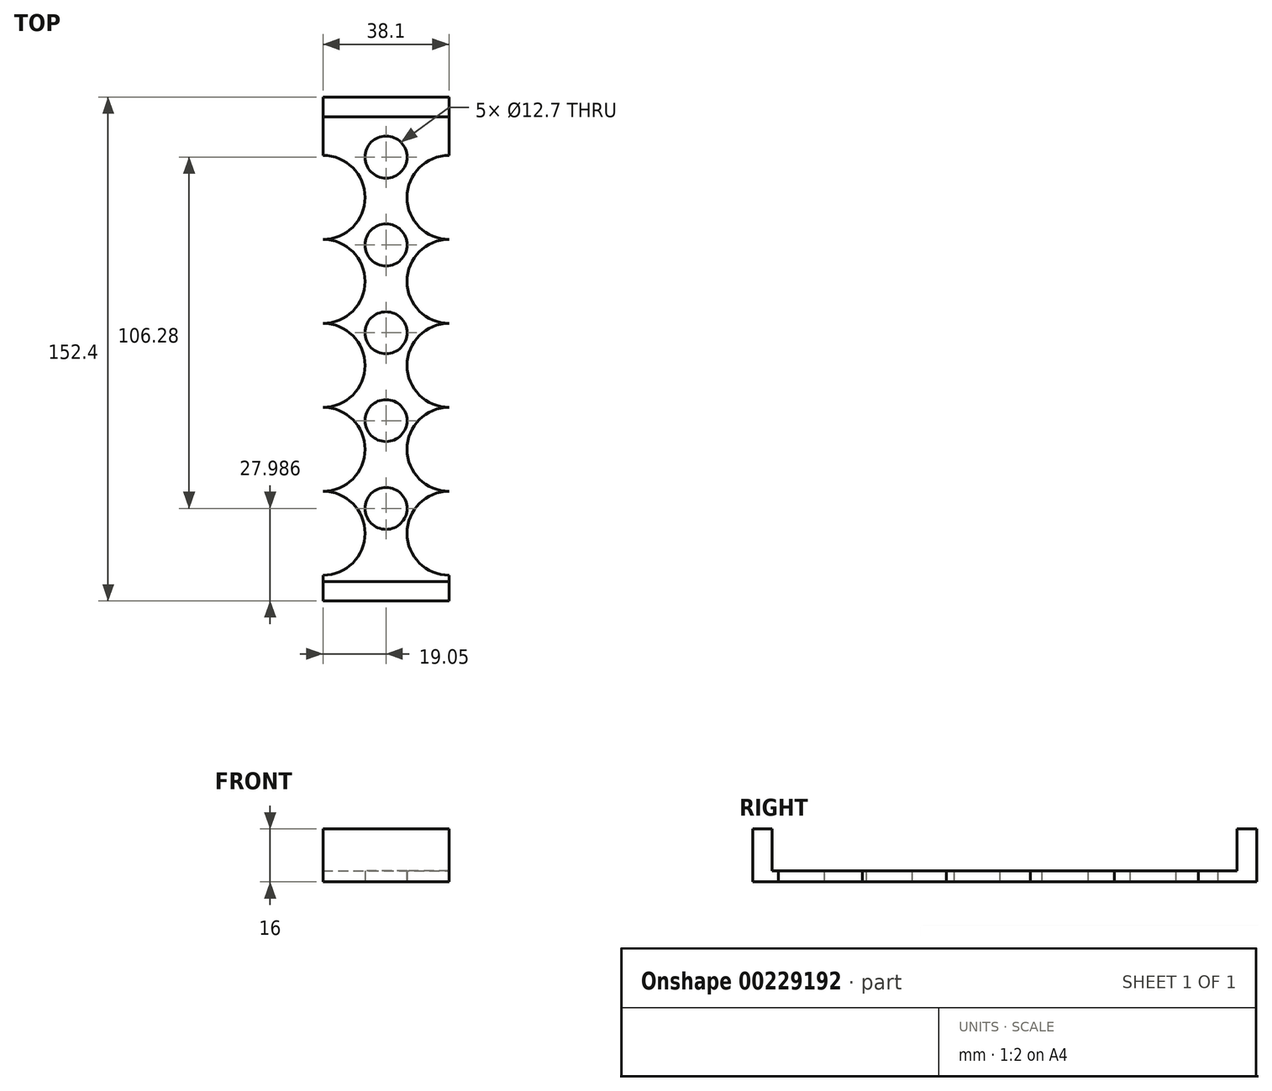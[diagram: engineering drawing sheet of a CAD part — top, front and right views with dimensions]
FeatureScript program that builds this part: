
annotation { "Feature Type Name" : "Feature", "Feature Type Description" : "" }
export const myFeature = defineFeature(function(context is Context, id is Id, definition is map)
    precondition{}
    {
        {
            var Q0;
            Q0=qCreatedBy(makeId("Top.planeOp"),FACE);
            var sketch = newSketch(context, id + "F0", { "sketchPlane" : qUnion([Q0])});
            skLineSegment(sketch, "E0.bottom", {"start": v(19.05, 76.2) * mm, "end": v(-19.05, 76.2) * mm});
            skLineSegment(sketch, "E0.top", {"start": v(19.05, -76.2) * mm, "end": v(-19.05, -76.2) * mm});
            skLineSegment(sketch, "E0.left", {"start": v(19.05, 76.2) * mm, "end": v(19.05, -76.2) * mm});
            skLineSegment(sketch, "E0.right", {"start": v(-19.05, 76.2) * mm, "end": v(-19.05, -76.2) * mm});
            skPoint(sketch, "E0.middle", {"position": v(0, 0) * mm});
            skCircle(sketch, "E1", {"center": v(0, 58.07) * mm, "radius": 6.35 * mm});
            skCircle(sketch, "E2.0.1.0", {"center": v(0, 31.5) * mm, "radius": 6.35 * mm});
            skCircle(sketch, "E2.0.2.0", {"center": v(0, 4.93) * mm, "radius": 6.35 * mm});
            skCircle(sketch, "E2.0.3.0", {"center": v(0, -21.64) * mm, "radius": 6.35 * mm});
            skCircle(sketch, "E2.0.4.0", {"center": v(0, -48.21) * mm, "radius": 6.35 * mm});
            skLineSegment(sketch, "E2.direction1", {"start": v(0, 58.07) * mm, "end": v(29.46, 58.07) * mm, "construction": true});
            skLineSegment(sketch, "E2.direction2", {"start": v(0, 58.07) * mm, "end": v(0, 31.5) * mm, "construction": true});
            skSolve(sketch);
        }
        {
            var Q0;
            Q0=makeQuery(id+"F0.imprint","IMPRINT",FACE,{"disambiguationData":[TD([[makeQuery(id+"F0.imprint","IMPRINT",EDGE,{"derivedFrom":sQuery(id+"F0.wireOp",EDGE,"E0.bottom")}),1.0]])]});
            extrude(context, id + "F1", {"entities" : qUnion([Q0]), "depth" : 3.3 * mm});
        }
        {
            var Q0;
            Q0=makeQuery(id+"F1.opExtrude","CAP_FACE",FACE,{"disambiguationData":[OSD([sQuery(id+"F0.wireOp",EDGE,"E0.bottom"),sQuery(id+"F0.wireOp",EDGE,"E0.top"),sQuery(id+"F0.wireOp",EDGE,"E0.left"),sQuery(id+"F0.wireOp",EDGE,"E0.right"),sQuery(id+"F0.wireOp",EDGE,"E1"),sQuery(id+"F0.wireOp",EDGE,"E2.0.1.0"),sQuery(id+"F0.wireOp",EDGE,"E2.0.2.0"),sQuery(id+"F0.wireOp",EDGE,"E2.0.3.0"),sQuery(id+"F0.wireOp",EDGE,"E2.0.4.0")])],"isStart":false});
            var sketch = newSketch(context, id + "F2", { "sketchPlane" : qUnion([Q0])});
            skLineSegment(sketch, "E3.bottom", {"start": v(-19.05, 76.2) * mm, "end": v(19.05, 76.2) * mm});
            skLineSegment(sketch, "E3.top", {"start": v(-19.05, 70.3) * mm, "end": v(19.05, 70.3) * mm});
            skLineSegment(sketch, "E3.left", {"start": v(-19.05, 76.2) * mm, "end": v(-19.05, 70.3) * mm});
            skLineSegment(sketch, "E3.right", {"start": v(19.05, 76.2) * mm, "end": v(19.05, 70.3) * mm});
            skLineSegment(sketch, "E4", {"start": v(-36.38, 0) * mm, "end": v(51.74, 0) * mm});
            skLineSegment(sketch, "E5.MirrorCS", {"start": v(-19.05, -76.2) * mm, "end": v(-19.05, -70.3) * mm});
            skLineSegment(sketch, "E6.MirrorCS", {"start": v(-19.05, -70.3) * mm, "end": v(19.05, -70.3) * mm});
            skLineSegment(sketch, "E7.MirrorCS", {"start": v(19.05, -76.2) * mm, "end": v(19.05, -70.3) * mm});
            skLineSegment(sketch, "E8.MirrorCS", {"start": v(-19.05, -76.2) * mm, "end": v(19.05, -76.2) * mm});
            skSolve(sketch);
        }
        {
            var Q0;
            Q0=makeQuery(id+"F2.imprint","IMPRINT",FACE,{"disambiguationData":[TD([[makeQuery(id+"F2.imprint","IMPRINT",EDGE,{"derivedFrom":sQuery(id+"F2.wireOp",EDGE,"E3.bottom")}),1.0]])]});
            var Q1;
            Q1=makeQuery(id+"F2.imprint","IMPRINT",FACE,{"disambiguationData":[TD([[makeQuery(id+"F2.imprint","IMPRINT",EDGE,{"derivedFrom":sQuery(id+"F2.wireOp",EDGE,"E5.MirrorCS")}),1.0]])]});
            extrude(context, id + "F3", {"entities" : qUnion([Q0, Q1]), "operationType" : NewBodyOperationType.ADD, "depth" : 12.7 * mm});
        }
        {
            var Q0;
            Q0=makeQuery(id+"F1.opExtrude","CAP_FACE",FACE,{"disambiguationData":[OSD([sQuery(id+"F0.wireOp",EDGE,"E0.bottom"),sQuery(id+"F0.wireOp",EDGE,"E0.top"),sQuery(id+"F0.wireOp",EDGE,"E0.left"),sQuery(id+"F0.wireOp",EDGE,"E0.right"),sQuery(id+"F0.wireOp",EDGE,"E1"),sQuery(id+"F0.wireOp",EDGE,"E2.0.1.0"),sQuery(id+"F0.wireOp",EDGE,"E2.0.2.0"),sQuery(id+"F0.wireOp",EDGE,"E2.0.3.0"),sQuery(id+"F0.wireOp",EDGE,"E2.0.4.0")])],"isStart":false});
            var sketch = newSketch(context, id + "F4", { "sketchPlane" : qUnion([Q0])});
            skCircle(sketch, "E9", {"center": v(-19.05, 45.87) * mm, "radius": 12.7 * mm});
            skCircle(sketch, "E10", {"center": v(19.05, 45.87) * mm, "radius": 12.7 * mm});
            skCircle(sketch, "E11.0.1.0", {"center": v(19.05, 20.47) * mm, "radius": 12.7 * mm});
            skCircle(sketch, "E11.0.1.1", {"center": v(-19.05, 20.47) * mm, "radius": 12.7 * mm});
            skCircle(sketch, "E11.0.2.0", {"center": v(19.05, -4.93) * mm, "radius": 12.7 * mm});
            skCircle(sketch, "E11.0.2.1", {"center": v(-19.05, -4.93) * mm, "radius": 12.7 * mm});
            skCircle(sketch, "E11.0.3.0", {"center": v(19.05, -30.33) * mm, "radius": 12.7 * mm});
            skCircle(sketch, "E11.0.3.1", {"center": v(-19.05, -30.33) * mm, "radius": 12.7 * mm});
            skCircle(sketch, "E11.0.4.0", {"center": v(19.05, -55.73) * mm, "radius": 12.7 * mm});
            skCircle(sketch, "E11.0.4.1", {"center": v(-19.05, -55.73) * mm, "radius": 12.7 * mm});
            skLineSegment(sketch, "E11.direction1", {"start": v(19.05, 45.87) * mm, "end": v(44.45, 45.87) * mm, "construction": true});
            skLineSegment(sketch, "E11.direction2", {"start": v(19.05, 45.87) * mm, "end": v(19.05, 20.47) * mm, "construction": true});
            skSolve(sketch);
        }
        {
            var Q0;
            {var subQ0=sQuery(id+"F4.wireOp",EDGE,"E9");var subQ1=makeQuery(id+"F1.opExtrude","CAP_EDGE",EDGE,{"disambiguationData":[OSD([sQuery(id+"F0.wireOp",EDGE,"E0.right")])],"isStart":false});var subQ2=makeQuery(id+"F4.imprint","INTERSECT",VERTEX,{"derivedFrom":[subQ1,subQ0]});Q0=makeQuery(id+"F4.imprint","IMPRINT",FACE,{"disambiguationData":[TD([[makeQuery(id+"F4.imprint","IMPRINT",EDGE,{"disambiguationData":[TD([[subQ2,1.0]])],"derivedFrom":subQ0}),1.0]])]});}
            var Q1;
            {var subQ0=sQuery(id+"F4.wireOp",EDGE,"E10");var subQ1=makeQuery(id+"F1.opExtrude","CAP_EDGE",EDGE,{"disambiguationData":[OSD([sQuery(id+"F0.wireOp",EDGE,"E0.left")])],"isStart":false});var subQ2=makeQuery(id+"F4.imprint","INTERSECT",VERTEX,{"derivedFrom":[subQ1,subQ0]});Q1=makeQuery(id+"F4.imprint","IMPRINT",FACE,{"disambiguationData":[TD([[makeQuery(id+"F4.imprint","IMPRINT",EDGE,{"disambiguationData":[TD([[subQ2,-1.0]])],"derivedFrom":subQ0}),1.0]])]});}
            var Q2;
            {var subQ0=sQuery(id+"F4.wireOp",EDGE,"E11.0.1.0");var subQ1=makeQuery(id+"F1.opExtrude","CAP_EDGE",EDGE,{"disambiguationData":[OSD([sQuery(id+"F0.wireOp",EDGE,"E0.left")])],"isStart":false});var subQ2=makeQuery(id+"F4.imprint","INTERSECT",VERTEX,{"derivedFrom":[subQ1,sQuery(id+"F4.wireOp",EDGE,"E10"),subQ0]});Q2=makeQuery(id+"F4.imprint","IMPRINT",FACE,{"disambiguationData":[TD([[makeQuery(id+"F4.imprint","IMPRINT",EDGE,{"disambiguationData":[TD([[subQ2,-1.0]])],"derivedFrom":subQ0}),1.0]])]});}
            var Q3;
            {var subQ0=sQuery(id+"F4.wireOp",EDGE,"E11.0.2.0");var subQ1=makeQuery(id+"F1.opExtrude","CAP_EDGE",EDGE,{"disambiguationData":[OSD([sQuery(id+"F0.wireOp",EDGE,"E0.left")])],"isStart":false});var subQ2=makeQuery(id+"F4.imprint","INTERSECT",VERTEX,{"derivedFrom":[subQ1,sQuery(id+"F4.wireOp",EDGE,"E11.0.1.0"),subQ0]});Q3=makeQuery(id+"F4.imprint","IMPRINT",FACE,{"disambiguationData":[TD([[makeQuery(id+"F4.imprint","IMPRINT",EDGE,{"disambiguationData":[TD([[subQ2,-1.0]])],"derivedFrom":subQ0}),1.0]])]});}
            var Q4;
            {var subQ0=sQuery(id+"F4.wireOp",EDGE,"E11.0.3.0");var subQ1=makeQuery(id+"F1.opExtrude","CAP_EDGE",EDGE,{"disambiguationData":[OSD([sQuery(id+"F0.wireOp",EDGE,"E0.left")])],"isStart":false});var subQ2=makeQuery(id+"F4.imprint","INTERSECT",VERTEX,{"derivedFrom":[subQ1,sQuery(id+"F4.wireOp",EDGE,"E11.0.2.0"),subQ0]});Q4=makeQuery(id+"F4.imprint","IMPRINT",FACE,{"disambiguationData":[TD([[makeQuery(id+"F4.imprint","IMPRINT",EDGE,{"disambiguationData":[TD([[subQ2,-1.0]])],"derivedFrom":subQ0}),1.0]])]});}
            var Q5;
            {var subQ0=sQuery(id+"F4.wireOp",EDGE,"E11.0.4.0");var subQ1=makeQuery(id+"F1.opExtrude","CAP_EDGE",EDGE,{"disambiguationData":[OSD([sQuery(id+"F0.wireOp",EDGE,"E0.left")])],"isStart":false});var subQ2=makeQuery(id+"F4.imprint","INTERSECT",VERTEX,{"derivedFrom":[subQ1,subQ0]});Q5=makeQuery(id+"F4.imprint","IMPRINT",FACE,{"disambiguationData":[TD([[makeQuery(id+"F4.imprint","IMPRINT",EDGE,{"disambiguationData":[TD([[subQ2,1.0]])],"derivedFrom":subQ0}),1.0]])]});}
            var Q6;
            {var subQ0=sQuery(id+"F4.wireOp",EDGE,"E11.0.4.1");var subQ1=makeQuery(id+"F1.opExtrude","CAP_EDGE",EDGE,{"disambiguationData":[OSD([sQuery(id+"F0.wireOp",EDGE,"E0.right")])],"isStart":false});var subQ2=makeQuery(id+"F4.imprint","INTERSECT",VERTEX,{"derivedFrom":[subQ1,subQ0]});Q6=makeQuery(id+"F4.imprint","IMPRINT",FACE,{"disambiguationData":[TD([[makeQuery(id+"F4.imprint","IMPRINT",EDGE,{"disambiguationData":[TD([[subQ2,-1.0]])],"derivedFrom":subQ0}),1.0]])]});}
            var Q7;
            {var subQ0=sQuery(id+"F4.wireOp",EDGE,"E11.0.3.1");var subQ1=makeQuery(id+"F1.opExtrude","CAP_EDGE",EDGE,{"disambiguationData":[OSD([sQuery(id+"F0.wireOp",EDGE,"E0.right")])],"isStart":false});var subQ2=makeQuery(id+"F4.imprint","INTERSECT",VERTEX,{"derivedFrom":[subQ1,sQuery(id+"F4.wireOp",EDGE,"E11.0.2.1"),subQ0]});Q7=makeQuery(id+"F4.imprint","IMPRINT",FACE,{"disambiguationData":[TD([[makeQuery(id+"F4.imprint","IMPRINT",EDGE,{"disambiguationData":[TD([[subQ2,1.0]])],"derivedFrom":subQ0}),1.0]])]});}
            var Q8;
            {var subQ0=sQuery(id+"F4.wireOp",EDGE,"E11.0.2.1");var subQ1=makeQuery(id+"F1.opExtrude","CAP_EDGE",EDGE,{"disambiguationData":[OSD([sQuery(id+"F0.wireOp",EDGE,"E0.right")])],"isStart":false});var subQ2=makeQuery(id+"F4.imprint","INTERSECT",VERTEX,{"derivedFrom":[subQ1,sQuery(id+"F4.wireOp",EDGE,"E11.0.1.1"),subQ0]});Q8=makeQuery(id+"F4.imprint","IMPRINT",FACE,{"disambiguationData":[TD([[makeQuery(id+"F4.imprint","IMPRINT",EDGE,{"disambiguationData":[TD([[subQ2,1.0]])],"derivedFrom":subQ0}),1.0]])]});}
            var Q9;
            {var subQ0=sQuery(id+"F4.wireOp",EDGE,"E11.0.1.1");var subQ1=makeQuery(id+"F1.opExtrude","CAP_EDGE",EDGE,{"disambiguationData":[OSD([sQuery(id+"F0.wireOp",EDGE,"E0.right")])],"isStart":false});var subQ2=makeQuery(id+"F4.imprint","INTERSECT",VERTEX,{"derivedFrom":[subQ1,sQuery(id+"F4.wireOp",EDGE,"E9"),subQ0]});Q9=makeQuery(id+"F4.imprint","IMPRINT",FACE,{"disambiguationData":[TD([[makeQuery(id+"F4.imprint","IMPRINT",EDGE,{"disambiguationData":[TD([[subQ2,1.0]])],"derivedFrom":subQ0}),1.0]])]});}
            extrude(context, id + "F5", {"entities" : qUnion([Q0, Q1, Q2, Q3, Q4, Q5, Q6, Q7, Q8, Q9]), "operationType" : NewBodyOperationType.REMOVE, "oppositeDirection" : true, "depth" : 25.4 * mm});
        }
    });
